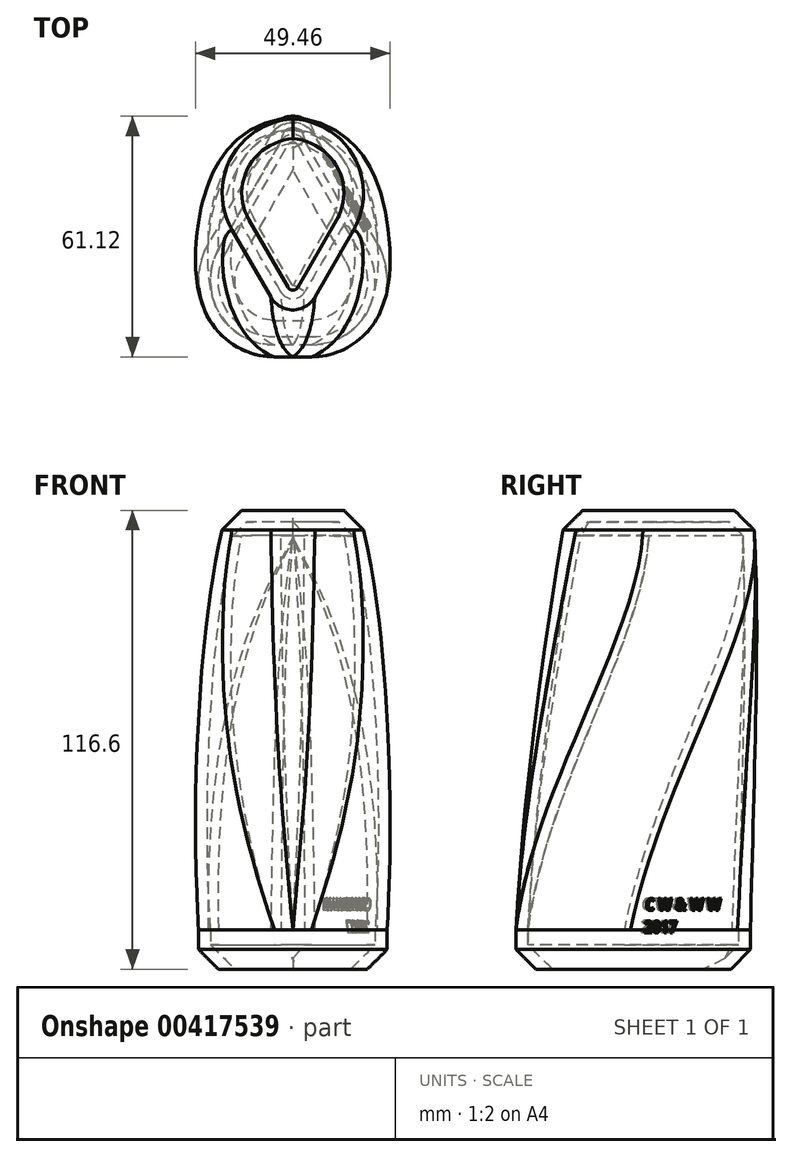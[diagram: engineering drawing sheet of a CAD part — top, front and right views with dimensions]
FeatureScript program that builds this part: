
annotation { "Feature Type Name" : "Feature", "Feature Type Description" : "" }
export const myFeature = defineFeature(function(context is Context, id is Id, definition is map)
    precondition{}
    {
        {
            var Q0;
            Q0=qCreatedBy(makeId("Top.planeOp"),FACE);
            var sketch = newSketch(context, id + "F0", { "sketchPlane" : qUnion([Q0])});
            skLineSegment(sketch, "E0", {"start": v(0, 33) * mm, "end": v(-38.1, -33) * mm});
            skLineSegment(sketch, "E1", {"start": v(-38.1, -33) * mm, "end": v(38.1, -33) * mm});
            skLineSegment(sketch, "E2", {"start": v(38.1, -33) * mm, "end": v(0, 33) * mm});
            skLineSegment(sketch, "E3", {"start": v(0, 33) * mm, "end": v(0, -33) * mm, "construction": true});
            skSolve(sketch);
        }
        {
            var Q0;
            Q0=qCreatedBy(makeId("Top.planeOp"),FACE);
            cPlane(context, id + "F1", {"entities" : qUnion([Q0]), "cplaneType" : CPlaneType.OFFSET, "offset" : 101.6 * mm, "width" : 152.4 * mm, "height" : 152.4 * mm});
        }
        {
            var Q0;
            Q0=qCreatedBy(id+"F1.planeOp",FACE);
            var sketch = newSketch(context, id + "F2", { "sketchPlane" : qUnion([Q0])});
            skLineSegment(sketch, "E4.0", {"start": v(0, 33) * mm, "end": v(-38.1, -33) * mm, "construction": true});
            skLineSegment(sketch, "E4.1", {"start": v(38.1, -33) * mm, "end": v(0, 33) * mm, "construction": true});
            skLineSegment(sketch, "E4.2", {"start": v(-38.1, -33) * mm, "end": v(38.1, -33) * mm, "construction": true});
            skLineSegment(sketch, "E5", {"start": v(-31.75, 27.5) * mm, "end": v(31.75, 27.5) * mm});
            skLineSegment(sketch, "E6", {"start": v(31.75, 27.5) * mm, "end": v(0, -27.5) * mm});
            skLineSegment(sketch, "E7", {"start": v(0, -27.5) * mm, "end": v(-31.75, 27.5) * mm});
            skLineSegment(sketch, "E8", {"start": v(0, 27.5) * mm, "end": v(0, -27.5) * mm, "construction": true});
            skSolve(sketch);
        }
        {
            var Q0;
            Q0=sQuery(id+"F0.wireOp",VERTEX,"E2.start");
            var Q1;
            Q1=sQuery(id+"F2.wireOp",VERTEX,"E7.start");
            var Q2;
            Q2=sQuery(id+"F0.wireOp",VERTEX,"E1.start");
            cPlane(context, id + "F3", {"entities" : qUnion([Q0, Q1, Q2]), "cplaneType" : CPlaneType.THREE_POINT, "offset" : 25.4 * mm, "width" : 152.4 * mm, "height" : 152.4 * mm});
        }
        {
            var Q0;
            Q0=qCreatedBy(id+"F3.planeOp",FACE);
            var sketch = newSketch(context, id + "F4", { "sketchPlane" : qUnion([Q0])});
            skLineSegment(sketch, "E9", {"start": v(0, -1.78) * mm, "end": v(0, 99.97) * mm});
            skSolve(sketch);
        }
        {
            var Q0;
            Q0=sQuery(id+"F0.wireOp",VERTEX,"E0.start");
            var Q1;
            Q1=sQuery(id+"F2.wireOp",VERTEX,"E6.start");
            var Q2;
            Q2=sQuery(id+"F2.wireOp",VERTEX,"E5.start");
            cPlane(context, id + "F5", {"entities" : qUnion([Q0, Q1, Q2]), "cplaneType" : CPlaneType.THREE_POINT, "offset" : 25.4 * mm, "width" : 152.4 * mm, "height" : 152.4 * mm});
        }
        {
            var Q0;
            Q0=qCreatedBy(id+"F5.planeOp",FACE);
            var sketch = newSketch(context, id + "F6", { "sketchPlane" : qUnion([Q0])});
            skLineSegment(sketch, "E10", {"start": v(0, 99.97) * mm, "end": v(0, -1.78) * mm});
            skSolve(sketch);
        }
        {
            var Q0;
            Q0=makeQuery(id+"F2.imprint","IMPRINT",FACE,{"disambiguationData":[TD([[makeQuery(id+"F2.imprint","IMPRINT",EDGE,{"derivedFrom":sQuery(id+"F2.wireOp",EDGE,"E5")}),-1.0]])]});
            var Q1;
            Q1=makeQuery(id+"F0.imprint","IMPRINT",FACE,{"disambiguationData":[TD([[makeQuery(id+"F0.imprint","IMPRINT",EDGE,{"derivedFrom":sQuery(id+"F0.wireOp",EDGE,"E0")}),1.0]])]});
            var Q2;
            Q2=sQuery(id+"F4.wireOp",EDGE,"E9");
            var Q3;
            Q3=sQuery(id+"F6.wireOp",EDGE,"E10");
            loft(context, id + "F7", {"addGuides" : true, "sheetProfilesArray" : [{ "sheetProfileEntities" : qUnion([Q0]) }, { "sheetProfileEntities" : qUnion([Q1]) }], "guidesArray" : [{ "guideEntities" : qUnion([Q2]), "guideDerivativeType" : LoftGuideDerivativeType.DEFAULT, "guideDerivativeMagnitude" : 1 }, { "guideEntities" : qUnion([Q3]), "guideDerivativeType" : LoftGuideDerivativeType.DEFAULT, "guideDerivativeMagnitude" : 1 }]});
        }
        {
            var Q0;
            Q0=makeQuery(id+"F7.opLoft","SWEPT_EDGE",EDGE,{"disambiguationData":[OSD([sQuery(id+"F4.wireOp",EDGE,"E9")])]});
            var Q1;
            Q1=makeQuery(id+"F7.opLoft","SWEPT_EDGE",EDGE,{"disambiguationData":[OSD([sQuery(id+"F6.wireOp",EDGE,"E10")])]});
            fillet(context, id + "F8", {"entities" : qUnion([Q0, Q1]), "radius" : 6.48 * mm, "tangentPropagation" : true, "allowEdgeOverflow" : false});
        }
        {
            var Q0;
            Q0=makeQuery(id+"F7.opLoft","SWEPT_EDGE",EDGE,{"disambiguationData":[OSD([sQuery(id+"F0.wireOp",EDGE,"E1"),sQuery(id+"F0.wireOp",EDGE,"E2"),sQuery(id+"F2.wireOp",EDGE,"E5"),sQuery(id+"F2.wireOp",EDGE,"E6")])]});
            var Q1;
            Q1=makeQuery(id+"F7.opLoft","SWEPT_EDGE",EDGE,{"disambiguationData":[OSD([sQuery(id+"F0.wireOp",EDGE,"E0"),sQuery(id+"F0.wireOp",EDGE,"E1"),sQuery(id+"F2.wireOp",EDGE,"E5"),sQuery(id+"F2.wireOp",EDGE,"E7")])]});
            fillet(context, id + "F9", {"entities" : qUnion([Q0, Q1]), "radius" : 19.05 * mm, "tangentPropagation" : true, "allowEdgeOverflow" : false});
        }
        {
            var Q0;
            {var subQ0=sQuery(id+"F2.wireOp",EDGE,"E6");var subQ1=sQuery(id+"F2.wireOp",EDGE,"E5");var subQ2=sQuery(id+"F0.wireOp",EDGE,"E2");var subQ3=sQuery(id+"F0.wireOp",EDGE,"E1");Q0=makeQuery(id+"F9.opFillet","BLEND_EDGE",EDGE,{"blendedFrom":[makeQuery(id+"F7.opLoft","SWEPT_EDGE",EDGE,{"disambiguationData":[OSD([subQ3,subQ2,subQ1,subQ0])]}),makeQuery(id+"F7.opLoft","SWEPT_FACE",FACE,{"disambiguationData":[OSD([subQ3,subQ2,subQ1,subQ0,sQuery(id+"F6.wireOp",EDGE,"E10")])]})],"blendedInto":[makeQuery(id+"F7.opLoft","SWEPT_FACE",FACE,{"disambiguationData":[OSD([subQ3,subQ2,subQ1,subQ0,sQuery(id+"F6.wireOp",EDGE,"E10")])]})]});}
            cPoint(context, id + "F10", {"entities" : qUnion([Q0]), "parameter" : 0.5});
        }
        {
            var Q0;
            Q0 = qCreatedBy(id + "F10" ,VERTEX);
            var Q1;
            {var subQ0=sQuery(id+"F0.wireOp",EDGE,"E1");var subQ1=sQuery(id+"F0.wireOp",EDGE,"E2");var subQ2=sQuery(id+"F6.wireOp",EDGE,"E10");Q1=makeQuery(id+"F8.opFillet","BLEND_VERTEX",VERTEX,{"blendedFrom":[makeQuery(id+"F7.opLoft","SWEPT_EDGE",EDGE,{"disambiguationData":[OSD([subQ2])]}),makeQuery(id+"F7.opLoft","SWEPT_FACE",FACE,{"disambiguationData":[OSD([subQ0,subQ1,sQuery(id+"F2.wireOp",EDGE,"E5"),sQuery(id+"F2.wireOp",EDGE,"E6"),subQ2])]}),makeQuery(id+"F7.opLoft","CAP_FACE",FACE,{"disambiguationData":[OSD([makeQuery(id+"F0.imprint","IMPRINT",FACE,{"disambiguationData":[TD([[makeQuery(id+"F0.imprint","IMPRINT",EDGE,{"derivedFrom":sQuery(id+"F0.wireOp",EDGE,"E0")}),1.0]])]})])],"isStart":true})],"blendedInto":[makeQuery(id+"F7.opLoft","SWEPT_FACE",FACE,{"disambiguationData":[OSD([subQ0,subQ1,sQuery(id+"F2.wireOp",EDGE,"E5"),sQuery(id+"F2.wireOp",EDGE,"E6"),subQ2])]}),makeQuery(id+"F7.opLoft","CAP_FACE",FACE,{"disambiguationData":[OSD([makeQuery(id+"F0.imprint","IMPRINT",FACE,{"disambiguationData":[TD([[makeQuery(id+"F0.imprint","IMPRINT",EDGE,{"derivedFrom":sQuery(id+"F0.wireOp",EDGE,"E0")}),1.0]])]})])],"isStart":true})]});}
            var Q2;
            {var subQ0=sQuery(id+"F0.wireOp",EDGE,"E1");var subQ1=sQuery(id+"F0.wireOp",EDGE,"E2");var subQ2=sQuery(id+"F2.wireOp",EDGE,"E6");var subQ3=sQuery(id+"F2.wireOp",EDGE,"E5");Q2=makeQuery(id+"F9.opFillet","BLEND_VERTEX",VERTEX,{"blendedFrom":[makeQuery(id+"F7.opLoft","SWEPT_EDGE",EDGE,{"disambiguationData":[OSD([subQ0,subQ1,subQ3,subQ2])]}),makeQuery(id+"F7.opLoft","SWEPT_FACE",FACE,{"disambiguationData":[OSD([subQ0,subQ1,subQ3,subQ2,sQuery(id+"F6.wireOp",EDGE,"E10")])]}),makeQuery(id+"F7.opLoft","CAP_FACE",FACE,{"disambiguationData":[OSD([makeQuery(id+"F0.imprint","IMPRINT",FACE,{"disambiguationData":[TD([[makeQuery(id+"F0.imprint","IMPRINT",EDGE,{"derivedFrom":sQuery(id+"F0.wireOp",EDGE,"E0")}),1.0]])]})])],"isStart":true})],"blendedInto":[makeQuery(id+"F7.opLoft","SWEPT_FACE",FACE,{"disambiguationData":[OSD([subQ0,subQ1,subQ3,subQ2,sQuery(id+"F6.wireOp",EDGE,"E10")])]}),makeQuery(id+"F7.opLoft","CAP_FACE",FACE,{"disambiguationData":[OSD([makeQuery(id+"F0.imprint","IMPRINT",FACE,{"disambiguationData":[TD([[makeQuery(id+"F0.imprint","IMPRINT",EDGE,{"derivedFrom":sQuery(id+"F0.wireOp",EDGE,"E0")}),1.0]])]})])],"isStart":true})]});}
            cPlane(context, id + "F11", {"entities" : qUnion([Q0, Q1, Q2]), "cplaneType" : CPlaneType.THREE_POINT, "offset" : 25.4 * mm, "width" : 152.4 * mm, "height" : 152.4 * mm});
        }
        {
            var Q0;
            Q0=qCreatedBy(id+"F11.planeOp",FACE);
            var sketch = newSketch(context, id + "F12", { "sketchPlane" : qUnion([Q0])});
            skText(sketch, "E11", { "text": "C W & W W\n2017\n", "fontName": "OpenSans-Bold.ttf"});
            skLineSegment(sketch, "E12", {"start": v(1.72, 1.7) * mm, "end": v(1.72, 6.7) * mm, "construction": true});
            skLineSegment(sketch, "E13", {"start": v(13.1, 0.99) * mm, "end": v(13.1, 5.99) * mm, "construction": true});
            const initialGuessF12  = {"E11": [-0.00966, 0.00743, 0.99799, -0.06338, 0.00304]};
            skSetInitialGuess(sketch, initialGuessF12);
            skSolve(sketch);
        }
        {
            var Q0;
            Q0=makeQuery(id+"F7.opLoft","CAP_FACE",FACE,{"disambiguationData":[OSD([makeQuery(id+"F0.imprint","IMPRINT",FACE,{"disambiguationData":[TD([[makeQuery(id+"F0.imprint","IMPRINT",EDGE,{"derivedFrom":sQuery(id+"F0.wireOp",EDGE,"E0")}),1.0]])]})])],"isStart":true});
            extrude(context, id + "F13", {"entities" : qUnion([Q0]), "operationType" : NewBodyOperationType.ADD, "depth" : 10 * mm});
        }
        {
            var Q0;
            Q0=makeQuery(id+"F7.opLoft","CAP_FACE",FACE,{"disambiguationData":[OSD([makeQuery(id+"F2.imprint","IMPRINT",FACE,{"disambiguationData":[TD([[makeQuery(id+"F2.imprint","IMPRINT",EDGE,{"derivedFrom":sQuery(id+"F2.wireOp",EDGE,"E5")}),-1.0]])]})])],"isStart":true});
            extrude(context, id + "F14", {"entities" : qUnion([Q0]), "operationType" : NewBodyOperationType.ADD, "depth" : 5 * mm});
        }
        {
            var Q0;
            Q0=makeQuery(id+"F14.opExtrude","CAP_EDGE",EDGE,{"disambiguationData":[OSD([sQuery(id+"F2.wireOp",EDGE,"E5"),sQuery(id+"F2.wireOp",EDGE,"E6"),sQuery(id+"F4.wireOp",EDGE,"E9")])],"isStart":false});
            var Q1;
            Q1=makeQuery(id+"F13.opExtrude","CAP_EDGE",EDGE,{"disambiguationData":[OSD([sQuery(id+"F0.wireOp",EDGE,"E1"),sQuery(id+"F0.wireOp",EDGE,"E2"),sQuery(id+"F6.wireOp",EDGE,"E10")])],"isStart":false});
            chamfer(context, id + "F15", {"entities" : qUnion([Q0, Q1]), "width" : 5 * mm, "tangentPropagation" : true});
        }
        {
            var Q0;
            Q0=makeQuery(id+"F13.opExtrude","CAP_FACE",FACE,{"disambiguationData":[OSD([makeQuery(id+"F0.imprint","IMPRINT",FACE,{"disambiguationData":[TD([[makeQuery(id+"F0.imprint","IMPRINT",EDGE,{"derivedFrom":sQuery(id+"F0.wireOp",EDGE,"E0")}),1.0]])]})])],"isStart":false});
            var Q1;
            Q1=makeQuery(id+"F7.opLoft","SWEPT_BODY",BODY,{"disambiguationData":[OSD([makeQuery(id+"F0.imprint","IMPRINT",FACE,{"disambiguationData":[TD([[makeQuery(id+"F0.imprint","IMPRINT",EDGE,{"derivedFrom":sQuery(id+"F0.wireOp",EDGE,"E0")}),1.0]])]}),makeQuery(id+"F2.imprint","IMPRINT",FACE,{"disambiguationData":[TD([[makeQuery(id+"F2.imprint","IMPRINT",EDGE,{"derivedFrom":sQuery(id+"F2.wireOp",EDGE,"E5")}),-1.0]])]}),sQuery(id+"F4.wireOp",EDGE,"E9"),sQuery(id+"F6.wireOp",EDGE,"E10")])]});
            shell(context, id + "F16", {"entities" : qUnion([Q0]), "parts" : qUnion([Q1]), "thickness" : 3 * mm});
        }
        {
            var Q0;
            Q0 = qSketchRegion(id + "F12", true);
            extrude(context, id + "F17", {"entities" : qUnion([Q0]), "operationType" : NewBodyOperationType.REMOVE, "oppositeDirection" : true, "depth" : 1.45 * mm, "hasSecondDirection" : true, "secondDirectionOppositeDirection" : false, "secondDirectionDepth" : 1 * mm});
        }
    });
